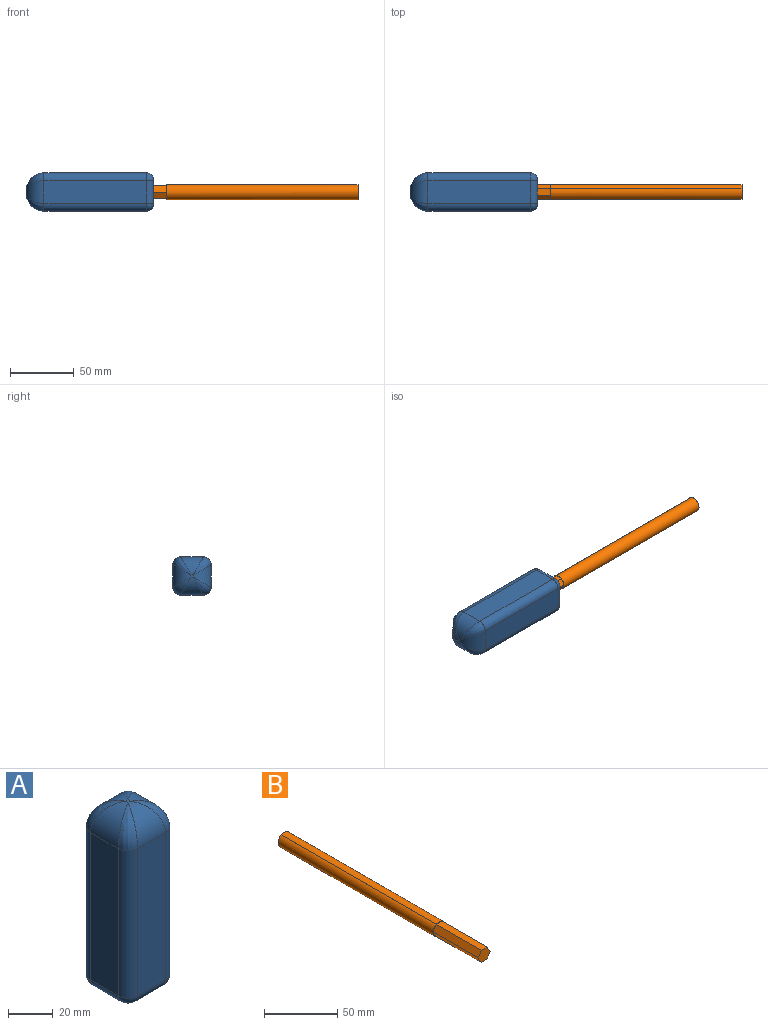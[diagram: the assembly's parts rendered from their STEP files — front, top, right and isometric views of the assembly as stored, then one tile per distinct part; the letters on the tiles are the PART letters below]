
ASSEMBLY  parts=2 mates=1
PART A: 33 faces, bbox 30x30x100 mm
  f0: plane 80.82x17.74mm, normal (1,0,0), area 1433.3mm2, adj f16,f21,f23,f30
  f1: plane 1.79x1.79mm, normal (0,0,1), area 3.2mm2, adj f13,f14,f15,f16
  f2: plane 80.82x17.74mm, normal (-1,0,0), area 1433.3mm2, adj f13,f17,f19,f27
  f3: plane 19.84x19.84mm, normal (0,0,-1), area 329.9mm2, adj f6,f7,f8,f9,f10,f11,f25,f26
  f4: plane 80.82x17.74mm, normal (0,-1,0), area 1433.3mm2, adj f14,f17,f21,f31
  f5: plane 80.82x17.74mm, normal (0,1,0), area 1433.3mm2, adj f15,f19,f23,f26
  f6: plane 33.02x4.26mm, normal (-0.87,0.5,0), area 162.3mm2, adj f3,f7,f11,f12
  f7: plane 33.02x4.92mm, normal (0,1,0), area 162.3mm2, adj f3,f6,f8,f12
  f8: plane 33.02x4.26mm, normal (0.87,0.5,0), area 162.3mm2, adj f3,f7,f9,f12
  f9: plane 33.02x4.26mm, normal (0.87,-0.5,0), area 162.3mm2, adj f3,f8,f10,f12
  f10: plane 33.02x4.92mm, normal (0,-1,0), area 162.3mm2, adj f3,f9,f11,f12
  f11: plane 33.02x4.26mm, normal (-0.87,-0.5,0), area 162.3mm2, adj f3,f6,f10,f12
  f12: plane 9.83x8.52mm, normal (0,0,-1), area 62.8mm2, adj f6,f7,f8,f9,f10,f11
  f13: cylinder r=14.1mm len=17.74mm, axis (0,1,0), area 264.6mm2, adj f1,f2,f18,f20
  f14: cylinder r=14.1mm len=17.74mm, axis (1,0,0), area 264.6mm2, adj f1,f4,f18,f22
  f15: cylinder r=14.1mm len=17.74mm, axis (-1,0,0), area 264.6mm2, adj f1,f5,f20,f24
  f16: cylinder r=14.1mm len=17.74mm, axis (0,-1,0), area 264.6mm2, adj f0,f1,f22,f24
  f17: cylinder r=6.13mm len=80.82mm, axis (0,0,1), area 778.4mm2, adj f2,f4,f18,f29
  f18: bspline ~16.72x14.1mm, area 143.6mm2, adj f13,f14,f17
  f19: cylinder r=6.13mm len=80.82mm, axis (0,0,-1), area 778.4mm2, adj f2,f5,f20,f25
  f20: bspline ~16.72x14.1mm, area 143.6mm2, adj f13,f15,f19
  f21: cylinder r=6.13mm len=80.82mm, axis (0,0,-1), area 778.4mm2, adj f0,f4,f22,f32
  f22: bspline ~16.72x14.1mm, area 143.6mm2, adj f14,f16,f21
  f23: cylinder r=6.13mm len=80.82mm, axis (0,0,1), area 778.4mm2, adj f0,f5,f24,f28
  f24: bspline ~16.72x14.1mm, area 143.6mm2, adj f15,f16,f23
  f25: torus R=1.05mm, axis (0,0,-1), area 53.7mm2, adj f3,f19,f26,f27
  f26: cylinder r=5.08mm len=17.74mm, axis (1,0,0), area 141.5mm2, adj f3,f5,f25,f28
  f27: cylinder r=5.08mm len=17.74mm, axis (0,-1,0), area 141.5mm2, adj f2,f3,f25,f29
  f28: torus R=1.05mm, axis (0,0,-1), area 53.7mm2, adj f3,f23,f26,f30
  f29: torus R=1.05mm, axis (0,0,-1), area 53.7mm2, adj f3,f17,f27,f31
  f30: cylinder r=5.08mm len=17.74mm, axis (0,1,0), area 141.5mm2, adj f0,f3,f28,f32
  f31: cylinder r=5.08mm len=17.74mm, axis (-1,0,0), area 141.5mm2, adj f3,f4,f29,f32
  f32: torus R=1.05mm, axis (0,0,-1), area 53.7mm2, adj f3,f21,f30,f31
PART B: 11 faces, bbox 11.6x193.7x11.6 mm
  f0: plane 43.69x4.98mm, normal (-0.88,0,-0.48), area 248.1mm2, adj f1,f5,f6,f7
  f1: plane 43.69x5.68mm, normal (-0.02,0,-1), area 248.1mm2, adj f0,f2,f6,f7
  f2: plane 43.69x4.85mm, normal (0.85,0,-0.52), area 248.1mm2, adj f1,f3,f6,f7
  f3: plane 43.69x4.98mm, normal (0.88,0,0.48), area 248.1mm2, adj f2,f4,f6,f7
  f4: plane 193.69x5.68mm, normal (0.02,0,1), area 249mm2, adj f3,f5,f6,f8,f9,f10
  f5: plane 193.69x4.85mm, normal (-0.85,0,0.52), area 249mm2, adj f0,f4,f6,f7,f9,f10
  f6: plane 11.35x9.96mm, normal (0,-1,0), area 83.8mm2, adj f0,f1,f2,f3,f4,f5
  f7: plane 11.58x10.9mm, normal (0,-1,0), area 18.7mm2, adj f0,f1,f2,f3,f5,f9
  f8: plane 5.67x0.81mm, normal (0,-1,0), area 2.8mm2, adj f4,f9
  f9: cylinder r=5.79mm len=150mm, axis (0,-1,0), area 5456.7mm2, adj f4,f5,f7,f8,f10
  f10: plane 11.58x11.58mm, normal (0,1,0), area 105.4mm2, adj f4,f5,f9
PLACE A rot(axis=(0,-1,0),90deg) t=(-43.76,-16.13,10.4)mm
PLACE B rot(axis=(0,0,-1),90deg) t=(44.49,-31.13,0.99)mm
MATE fastened B.f6 <-> A.f12  axis (-1,0,0) through (0.8,-31.13,0.99)mm
